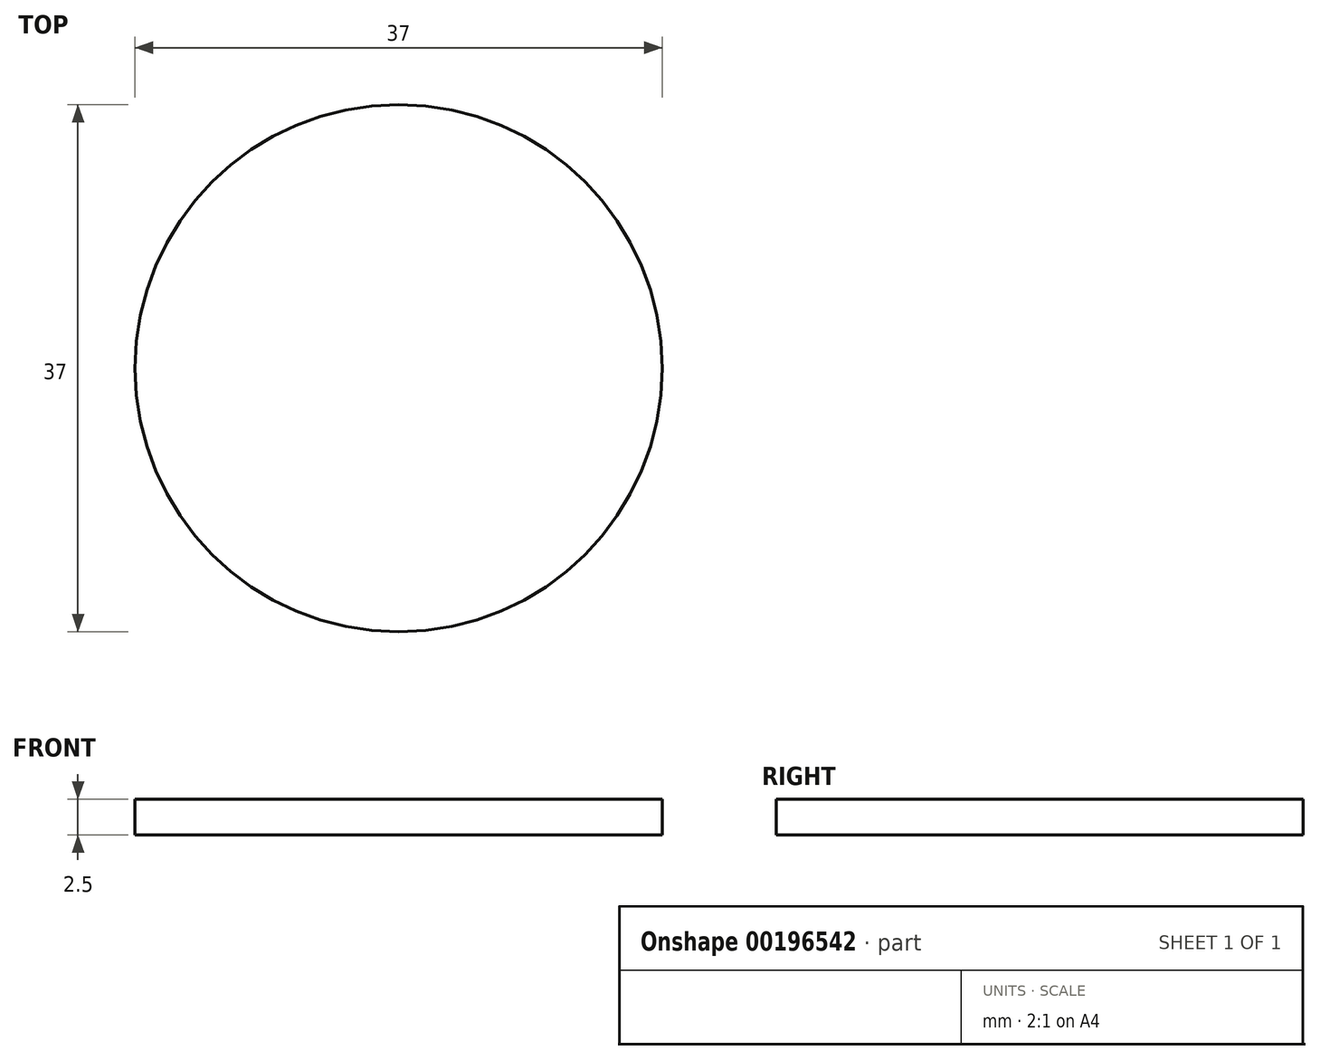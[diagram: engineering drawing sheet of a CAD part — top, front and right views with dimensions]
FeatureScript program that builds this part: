
annotation { "Feature Type Name" : "Feature", "Feature Type Description" : "" }
export const myFeature = defineFeature(function(context is Context, id is Id, definition is map)
    precondition{}
    {
        {
            var Q0;
            Q0=qCreatedBy(makeId("Top.planeOp"),FACE);
            var sketch = newSketch(context, id + "F0", { "sketchPlane" : qUnion([Q0])});
            skCircle(sketch, "E0", {"center": v(0, 0) * mm, "radius": 18.5 * mm});
            skSolve(sketch);
        }
        {
            var Q0;
            Q0 = qSketchRegion(id + "F0", true);
            extrude(context, id + "F1", {"entities" : qUnion([Q0]), "depth" : 2.5 * mm});
        }
    });
